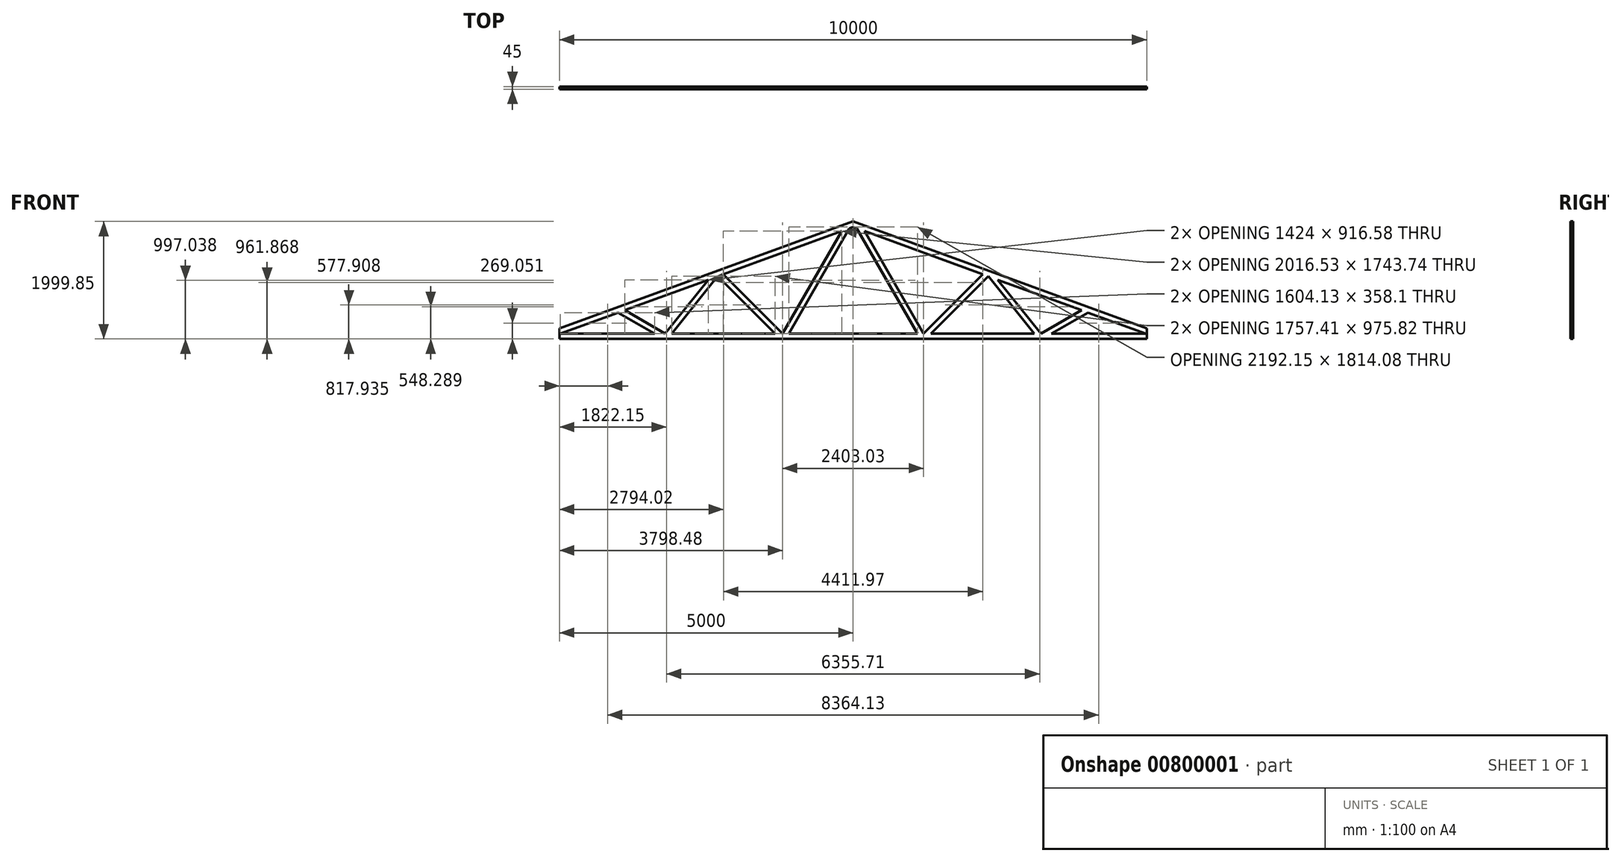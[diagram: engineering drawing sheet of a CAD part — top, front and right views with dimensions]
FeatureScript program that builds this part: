
annotation { "Feature Type Name" : "Feature", "Feature Type Description" : "" }
export const myFeature = defineFeature(function(context is Context, id is Id, definition is map)
    precondition{}
    {
        {
            var Q0;
            Q0=qCreatedBy(makeId("Front.planeOp"),FACE);
            var sketch = newSketch(context, id + "F0", { "sketchPlane" : qUnion([Q0])});
            skLineSegment(sketch, "E0", {"start": v(-5000, 0) * mm, "end": v(0, 1819.85) * mm});
            skLineSegment(sketch, "E1", {"start": v(0, 1819.85) * mm, "end": v(5000, 0) * mm});
            skLineSegment(sketch, "E2", {"start": v(5000, 0) * mm, "end": v(-5000, 0) * mm});
            skSolve(sketch);
        }
        {
            var Q0;
            Q0 = qSketchRegion(id + "F0", true);
            extrude(context, id + "F1", {"entities" : qUnion([Q0]), "endBound" : BoundingType.SYMMETRIC, "depth" : 45 * mm, "offsetDistance" : 25 * mm});
        }
        {
            var Q0;
            Q0=makeQuery(id+"F1.opExtrude","SWEPT_FACE",FACE,{"disambiguationData":[OSD([sQuery(id+"F0.wireOp",EDGE,"E2")])]});
            extrude(context, id + "F2", {"entities" : qUnion([Q0]), "operationType" : NewBodyOperationType.ADD, "depth" : 180 * mm, "offsetDistance" : 25 * mm});
        }
        {
            var Q0;
            {var subQ0=sQuery(id+"F0.wireOp",EDGE,"E2");Q0=makeQuery(id+"F2.boolean.opBoolean","MERGE",FACE,{"derivedFrom":[makeQuery(id+"F1.opExtrude","CAP_FACE",FACE,{"disambiguationData":[OSD([sQuery(id+"F0.wireOp",EDGE,"E0"),sQuery(id+"F0.wireOp",EDGE,"E1"),subQ0])],"isStart":false}),makeQuery(id+"F2.opExtrude","SWEPT_FACE",FACE,{"disambiguationData":[OSD([subQ0]),TDD([makeQuery(id+"F1.opExtrude","CAP_EDGE",EDGE,{"disambiguationData":[OSD([subQ0])],"isStart":false})])]})]});}
            var sketch = newSketch(context, id + "F3", { "sketchPlane" : qUnion([Q0])});
            skLineSegment(sketch, "E3.0", {"start": v(4984.13, -90) * mm, "end": v(3380, -90) * mm});
            skLineSegment(sketch, "E4.0", {"start": v(-4984.13, -90) * mm, "end": v(-4000.25, 268.1) * mm});
            skLineSegment(sketch, "E5", {"start": v(-193.25, 1653.74) * mm, "end": v(-1200, -90) * mm});
            skLineSegment(sketch, "E6", {"start": v(-1200, -90) * mm, "end": v(-2209.78, 919.78) * mm});
            skLineSegment(sketch, "E7", {"start": v(-3200, -90) * mm, "end": v(-3889.85, 308.29) * mm});
            skLineSegment(sketch, "E8.0", {"start": v(-61.68, 1701.62) * mm, "end": v(-1096.08, -90) * mm});
            skLineSegment(sketch, "E9.0", {"start": v(-1327.28, -90) * mm, "end": v(-2303.1, 885.82) * mm});
            skLineSegment(sketch, "E10", {"start": v(-2303.1, 885.82) * mm, "end": v(-3084.69, -90) * mm});
            skLineSegment(sketch, "E11.0", {"start": v(-2465.86, 826.58) * mm, "end": v(-3200, -90) * mm});
            skLineSegment(sketch, "E12.0", {"start": v(-3380, -90) * mm, "end": v(-4000.25, 268.1) * mm});
            skLineSegment(sketch, "E13.trimOffspring", {"start": v(-3380, -90) * mm, "end": v(-4984.13, -90) * mm});
            skLineSegment(sketch, "E14.trimOffspring", {"start": v(-3889.85, 308.29) * mm, "end": v(-2465.86, 826.58) * mm});
            skLineSegment(sketch, "E15.trimOffspring", {"start": v(-2209.78, 919.78) * mm, "end": v(-193.25, 1653.74) * mm});
            skLineSegment(sketch, "E16.trimOffspring", {"start": v(-1327.28, -90) * mm, "end": v(-3084.69, -90) * mm});
            skLineSegment(sketch, "E17.trimOffspring", {"start": v(-61.68, 1701.62) * mm, "end": v(0, 1724.08) * mm});
            skLineSegment(sketch, "E18", {"start": v(0, 1819.85) * mm, "end": v(0, 2472.65) * mm, "construction": true});
            skLineSegment(sketch, "E19.MirrorCS", {"start": v(61.68, 1701.62) * mm, "end": v(0, 1724.08) * mm});
            skLineSegment(sketch, "E20.MirrorCS", {"start": v(1327.28, -90) * mm, "end": v(3084.69, -90) * mm});
            skLineSegment(sketch, "E21.MirrorCS", {"start": v(3889.85, 308.29) * mm, "end": v(2465.86, 826.58) * mm});
            skLineSegment(sketch, "E22.MirrorCS", {"start": v(-5000, -90) * mm, "end": v(-3380, -90) * mm});
            skLineSegment(sketch, "E23.MirrorCS", {"start": v(2209.78, 919.78) * mm, "end": v(193.25, 1653.74) * mm});
            skLineSegment(sketch, "E24.MirrorCS", {"start": v(2303.1, 885.82) * mm, "end": v(3084.69, -90) * mm});
            skLineSegment(sketch, "E25.MirrorCS", {"start": v(1327.28, -90) * mm, "end": v(2303.1, 885.82) * mm});
            skLineSegment(sketch, "E26.MirrorCS", {"start": v(61.68, 1701.62) * mm, "end": v(1096.08, -90) * mm});
            skLineSegment(sketch, "E27.MirrorCS", {"start": v(3200, -90) * mm, "end": v(3889.85, 308.29) * mm});
            skLineSegment(sketch, "E28.MirrorCS", {"start": v(3380, -90) * mm, "end": v(4000.25, 268.1) * mm});
            skLineSegment(sketch, "E29.MirrorCS", {"start": v(1200, -90) * mm, "end": v(2209.78, 919.78) * mm});
            skLineSegment(sketch, "E30.MirrorCS", {"start": v(4984.13, -90) * mm, "end": v(4000.25, 268.1) * mm});
            skLineSegment(sketch, "E31.MirrorCS", {"start": v(3380, -90) * mm, "end": v(4984.13, -90) * mm});
            skLineSegment(sketch, "E32.MirrorCS", {"start": v(2465.86, 826.58) * mm, "end": v(3200, -90) * mm});
            skLineSegment(sketch, "E33.trimOffspring", {"start": v(-1096.08, -90) * mm, "end": v(1096.08, -90) * mm});
            skLineSegment(sketch, "E34.trimOffspring", {"start": v(1096.08, -90) * mm, "end": v(-1096.08, -90) * mm});
            skLineSegment(sketch, "E35.trimOffspring", {"start": v(3084.69, -90) * mm, "end": v(1327.28, -90) * mm});
            skLineSegment(sketch, "E36.trimOffspring", {"start": v(-3084.69, -90) * mm, "end": v(-1327.28, -90) * mm});
            skLineSegment(sketch, "E37", {"start": v(193.25, 1653.74) * mm, "end": v(1200, -90) * mm});
            skPoint(sketch, "E38.orphan", {"position": v(5000, -90) * mm});
            skPoint(sketch, "E39.orphan", {"position": v(-30.78, 1735.28) * mm});
            skPoint(sketch, "E40.orphan", {"position": v(30.78, 1735.28) * mm});
            skSolve(sketch);
        }
        {
            var Q0;
            {var subQ0=sQuery(id+"F3.wireOp",EDGE,"E4.0");Q0=makeQuery(id+"F3.imprint","IMPRINT",FACE,{"disambiguationData":[TD([[makeQuery(id+"F3.imprint","IMPRINT",EDGE,{"derivedFrom":subQ0}),-1.0]])]});}
            var Q1;
            Q1=makeQuery(id+"F3.imprint","IMPRINT",FACE,{"disambiguationData":[TD([[makeQuery(id+"F3.imprint","IMPRINT",EDGE,{"derivedFrom":sQuery(id+"F3.wireOp",EDGE,"E5")}),-1.0]])]});
            var Q2;
            Q2=makeQuery(id+"F3.imprint","IMPRINT",FACE,{"disambiguationData":[TD([[makeQuery(id+"F3.imprint","IMPRINT",EDGE,{"derivedFrom":sQuery(id+"F3.wireOp",EDGE,"E8.0")}),1.0]])]});
            var Q3;
            Q3=makeQuery(id+"F3.imprint","IMPRINT",FACE,{"disambiguationData":[TD([[makeQuery(id+"F3.imprint","IMPRINT",EDGE,{"derivedFrom":sQuery(id+"F3.wireOp",EDGE,"E9.0")}),1.0]])]});
            var Q4;
            Q4=makeQuery(id+"F3.imprint","IMPRINT",FACE,{"disambiguationData":[TD([[makeQuery(id+"F3.imprint","IMPRINT",EDGE,{"derivedFrom":sQuery(id+"F3.wireOp",EDGE,"E21.MirrorCS")}),1.0]])]});
            var Q5;
            Q5=makeQuery(id+"F3.imprint","IMPRINT",FACE,{"disambiguationData":[TD([[makeQuery(id+"F3.imprint","IMPRINT",EDGE,{"derivedFrom":sQuery(id+"F3.wireOp",EDGE,"E23.MirrorCS")}),1.0]])]});
            var Q6;
            Q6=makeQuery(id+"F3.imprint","IMPRINT",FACE,{"disambiguationData":[TD([[makeQuery(id+"F3.imprint","IMPRINT",EDGE,{"derivedFrom":sQuery(id+"F3.wireOp",EDGE,"E24.MirrorCS")}),-1.0]])]});
            var Q7;
            Q7=makeQuery(id+"F3.imprint","IMPRINT",FACE,{"disambiguationData":[TD([[makeQuery(id+"F3.imprint","IMPRINT",EDGE,{"derivedFrom":sQuery(id+"F3.wireOp",EDGE,"E28.MirrorCS")}),-1.0]])]});
            var Q8;
            Q8=makeQuery(id+"F3.imprint","IMPRINT",FACE,{"disambiguationData":[TD([[makeQuery(id+"F3.imprint","IMPRINT",EDGE,{"derivedFrom":sQuery(id+"F3.wireOp",EDGE,"E7")}),-1.0]])]});
            extrude(context, id + "F4", {"entities" : qUnion([Q0, Q1, Q2, Q3, Q4, Q5, Q6, Q7, Q8]), "operationType" : NewBodyOperationType.REMOVE, "endBound" : BoundingType.THROUGH_ALL, "oppositeDirection" : true, "depth" : 25 * mm, "offsetDistance" : 25 * mm});
        }
    });
